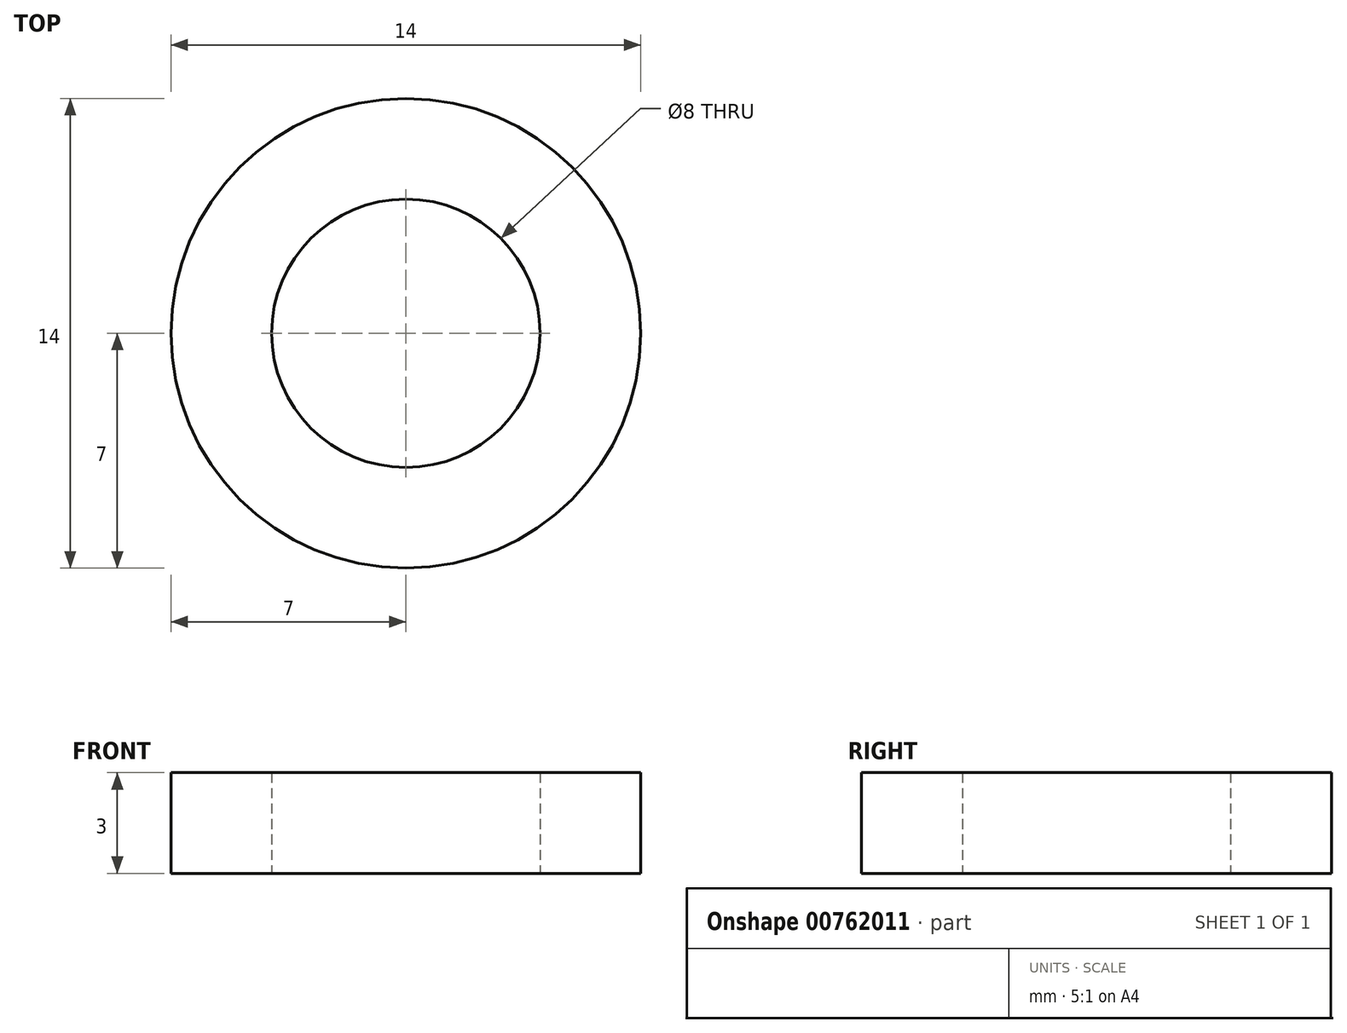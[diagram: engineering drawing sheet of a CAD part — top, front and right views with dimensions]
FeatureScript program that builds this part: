
annotation { "Feature Type Name" : "Feature", "Feature Type Description" : "" }
export const myFeature = defineFeature(function(context is Context, id is Id, definition is map)
    precondition{}
    {
        {
            var Q0;
            Q0=qCreatedBy(makeId("Top.planeOp"),FACE);
            var sketch = newSketch(context, id + "F0", { "sketchPlane" : qUnion([Q0])});
            skCircle(sketch, "E0", {"center": v(0, 0) * mm, "radius": 7 * mm});
            skCircle(sketch, "E1", {"center": v(0, 0) * mm, "radius": 4 * mm});
            skSolve(sketch);
        }
        {
            var Q0;
            Q0 = qSketchRegion(id + "F0", true);
            extrude(context, id + "F1", {"entities" : qUnion([Q0]), "depth" : 3 * mm, "offsetDistance" : 25 * mm});
        }
    });
